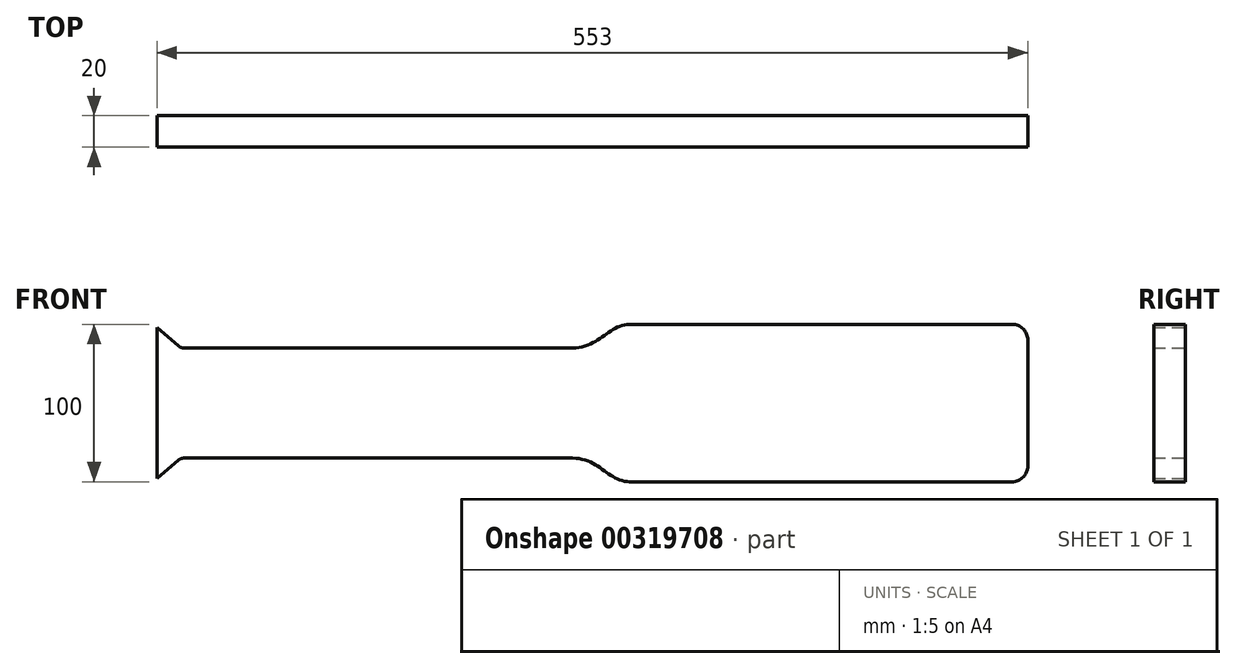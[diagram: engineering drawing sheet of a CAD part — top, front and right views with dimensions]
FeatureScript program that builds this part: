
annotation { "Feature Type Name" : "Feature", "Feature Type Description" : "" }
export const myFeature = defineFeature(function(context is Context, id is Id, definition is map)
    precondition{}
    {
        {
            var Q0;
            Q0=qCreatedBy(makeId("Front.planeOp"),FACE);
            var sketch = newSketch(context, id + "F0", { "sketchPlane" : qUnion([Q0])});
            skLineSegment(sketch, "E0.bottom", {"start": v(-300, 35) * mm, "end": v(151.53, 35) * mm});
            skLineSegment(sketch, "E0.top", {"start": v(-300, -35) * mm, "end": v(151.53, -35) * mm});
            skLineSegment(sketch, "E0.left", {"start": v(-300, 35) * mm, "end": v(-300, -35) * mm});
            skLineSegment(sketch, "E0.right", {"start": v(151.53, 35) * mm, "end": v(151.53, -35) * mm});
            skLineSegment(sketch, "E1.bottom", {"start": v(253, 50) * mm, "end": v(0, 50) * mm});
            skLineSegment(sketch, "E1.top", {"start": v(253, -50) * mm, "end": v(0, -50) * mm});
            skLineSegment(sketch, "E1.left", {"start": v(253, 50) * mm, "end": v(253, -50) * mm});
            skLineSegment(sketch, "E1.right", {"start": v(0, 50) * mm, "end": v(0, -50) * mm});
            skPoint(sketch, "E1.middle", {"position": v(126.5, 0) * mm});
            skLineSegment(sketch, "E2", {"start": v(-300, 35) * mm, "end": v(-300, 48) * mm});
            skLineSegment(sketch, "E3", {"start": v(-300, 48) * mm, "end": v(-300, -48) * mm});
            skLineSegment(sketch, "E4", {"start": v(-300, 48) * mm, "end": v(-285, 35) * mm});
            skLineSegment(sketch, "E5", {"start": v(-300, -48) * mm, "end": v(-285, -35) * mm});
            skPoint(sketch, "E6", {"position": v(-74.23, 35) * mm});
            skFitSpline(sketch, "E7", {"points": [v(0, 50) * mm, v(-36.25, 35) * mm], "startDerivative": vector(-39.3, 0) * mm, "endDerivative": vector(-51.43, 0) * mm});
            skFitSpline(sketch, "E8", {"points": [v(-36.25, -35) * mm, v(0, -50) * mm], "startDerivative": vector(51.43, 0) * mm, "endDerivative": vector(39.3, 0) * mm});
            skSolve(sketch);
        }
        {
            var Q0;
            Q0 = qSketchRegion(id + "F0", true);
            var Q1;
            {var subQ0=sQuery(id+"F0.wireOp",EDGE,"E1.right");var subQ1=sQuery(id+"F0.wireOp",EDGE,"E0.bottom");var subQ2=makeQuery(id+"F0.imprint","INTERSECT",VERTEX,{"derivedFrom":[subQ1,subQ0]});Q1=makeQuery(id+"F0.imprint","IMPRINT",FACE,{"disambiguationData":[TD([[makeQuery(id+"F0.imprint","IMPRINT",EDGE,{"disambiguationData":[TD([[subQ2,-1.0]])],"derivedFrom":subQ1}),-1.0]])]});}
            var Q2;
            {var subQ0=sQuery(id+"F0.wireOp",EDGE,"E0.right");Q2=makeQuery(id+"F0.imprint","IMPRINT",FACE,{"disambiguationData":[TD([[makeQuery(id+"F0.imprint","IMPRINT",EDGE,{"derivedFrom":subQ0}),-1.0]])]});}
            extrude(context, id + "F1", {"entities" : qUnion([Q0, Q1, Q2]), "depth" : 20 * mm, "symmetric" : true});
        }
        {
            var Q0;
            Q0=makeQuery(id+"F1.opExtrude","SWEPT_EDGE",EDGE,{"disambiguationData":[OSD([sQuery(id+"F0.wireOp",EDGE,"E1.bottom"),sQuery(id+"F0.wireOp",EDGE,"E1.left")])]});
            var Q1;
            Q1=makeQuery(id+"F1.opExtrude","SWEPT_EDGE",EDGE,{"disambiguationData":[OSD([sQuery(id+"F0.wireOp",EDGE,"E1.top"),sQuery(id+"F0.wireOp",EDGE,"E1.left")])]});
            fillet(context, id + "F2", {"entities" : qUnion([Q0, Q1]), "radius" : 10 * mm, "tangentPropagation" : true, "allowEdgeOverflow" : false});
        }
        {
            var Q0;
            Q0=makeQuery(id+"F1.opExtrude","SWEPT_EDGE",EDGE,{"disambiguationData":[OSD([sQuery(id+"F0.wireOp",EDGE,"E0.bottom"),sQuery(id+"F0.wireOp",EDGE,"E4")])]});
            fillet(context, id + "F3", {"entities" : qUnion([Q0]), "radius" : 5 * mm, "tangentPropagation" : true, "allowEdgeOverflow" : false});
        }
        {
            var Q0;
            Q0=makeQuery(id+"F1.opExtrude","SWEPT_EDGE",EDGE,{"disambiguationData":[OSD([sQuery(id+"F0.wireOp",EDGE,"E0.top"),sQuery(id+"F0.wireOp",EDGE,"E5")])]});
            fillet(context, id + "F4", {"entities" : qUnion([Q0]), "radius" : 5 * mm, "tangentPropagation" : true, "allowEdgeOverflow" : false});
        }
    });
